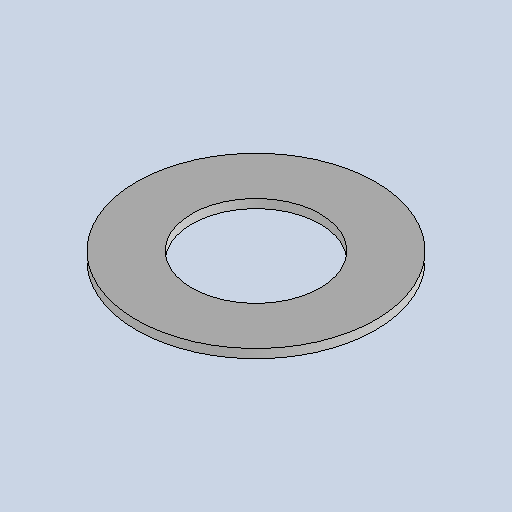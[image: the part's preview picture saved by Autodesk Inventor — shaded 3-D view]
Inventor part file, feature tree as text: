
AUTODESK INVENTOR PART (.ipt)
format: ipt  version: 2025.1 (Build 291241020, 241B)  size: 177,664 bytes
history: native  units: mm
features: other x2, sheet_metal_op x1, sketch x1
ambient origin geometry x8: Origin, YZ Plane, XZ Plane, XY Plane, X Axis, Y Axis, Z Axis, Center Point
bodies: Body1 (feature_tree)
feature tree (4):
  sheet_metal_op  "Face2"
  sketch  "Sketch2"  dims[d14=4.0mm d25=58.0mm d27=108.0mm]
  other  "Plate2"
  other  "Definition1"
